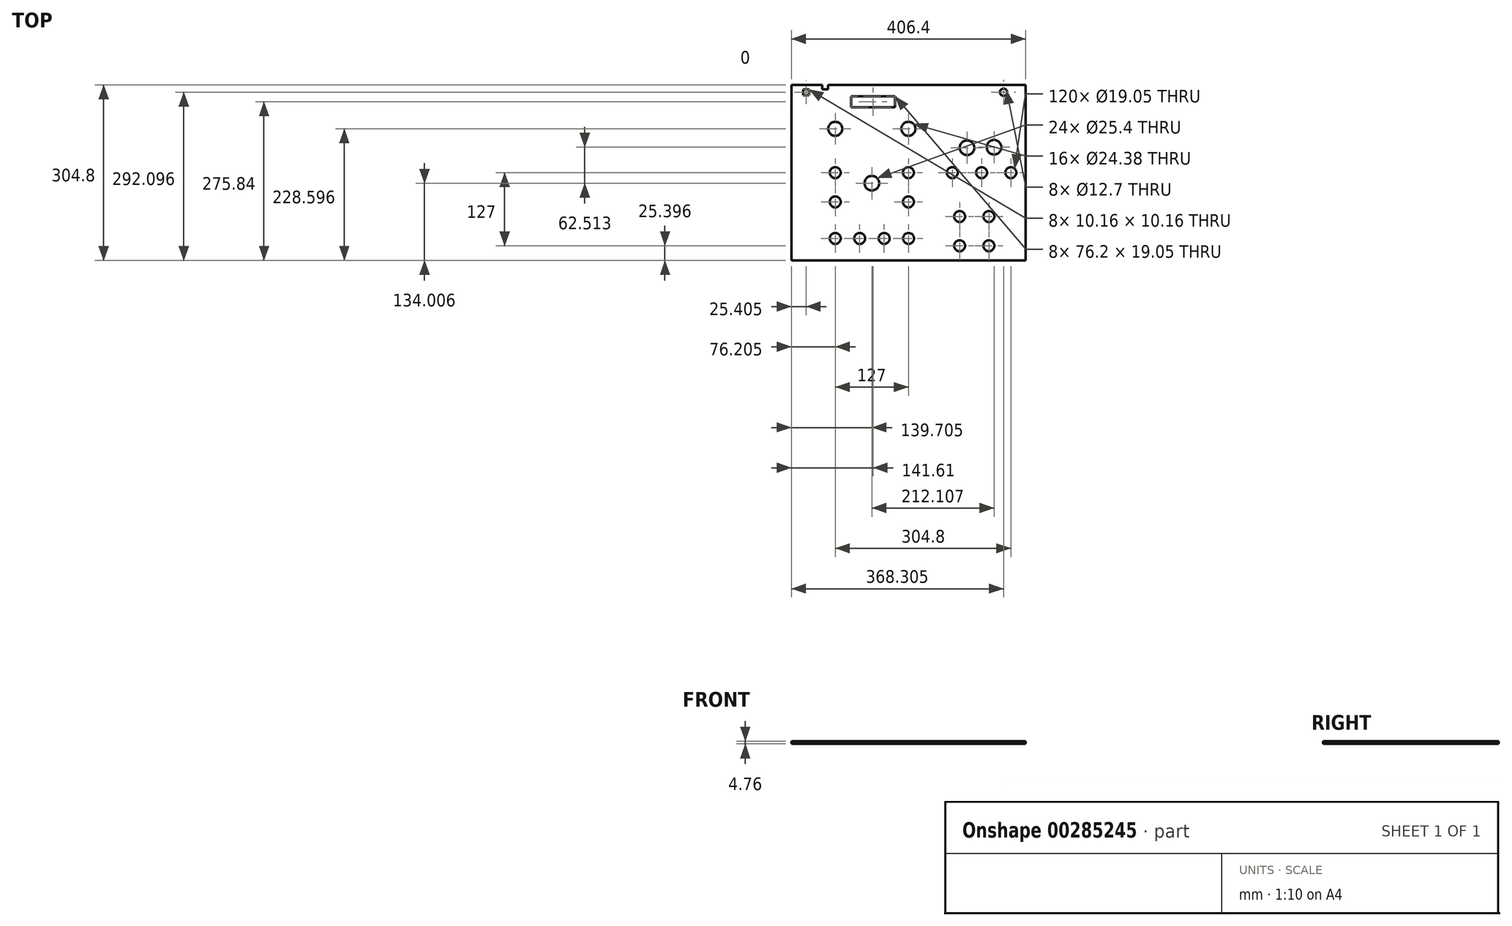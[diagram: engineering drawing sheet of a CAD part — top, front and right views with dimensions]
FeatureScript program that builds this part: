
annotation { "Feature Type Name" : "Feature", "Feature Type Description" : "" }
export const myFeature = defineFeature(function(context is Context, id is Id, definition is map)
    precondition{}
    {
        {
            var Q0;
            Q0=qCreatedBy(makeId("Top.planeOp"),FACE);
            var sketch = newSketch(context, id + "F0", { "sketchPlane" : qUnion([Q0])});
            skLineSegment(sketch, "E0.bottom", {"start": v(-218.92, 163.26) * mm, "end": v(187.48, 163.26) * mm});
            skLineSegment(sketch, "E0.top", {"start": v(-218.92, -141.54) * mm, "end": v(187.48, -141.54) * mm});
            skLineSegment(sketch, "E0.left", {"start": v(-218.92, 163.26) * mm, "end": v(-218.92, -141.54) * mm});
            skLineSegment(sketch, "E0.right", {"start": v(187.48, 163.26) * mm, "end": v(187.48, -141.54) * mm});
            skSolve(sketch);
        }
        {
            var Q0;
            Q0=makeQuery(id+"F0.imprint","IMPRINT",FACE,{"disambiguationData":[TD([[makeQuery(id+"F0.imprint","IMPRINT",EDGE,{"derivedFrom":sQuery(id+"F0.wireOp",EDGE,"E0.bottom")}),-1.0]])]});
            extrude(context, id + "F1", {"entities" : qUnion([Q0]), "depth" : 4.76 * mm});
        }
        {
            var Q0;
            Q0=qCreatedBy(makeId("Top.planeOp"),FACE);
            var sketch = newSketch(context, id + "F2", { "sketchPlane" : qUnion([Q0])});
            skCircle(sketch, "E1", {"center": v(-142.72, 87.06) * mm, "radius": 12.2 * mm});
            skLineSegment(sketch, "E2", {"start": v(-142.72, 87.06) * mm, "end": v(-142.72, -142.08) * mm, "construction": true});
            skCircle(sketch, "E3", {"center": v(-142.72, 10.86) * mm, "radius": 9.53 * mm});
            skCircle(sketch, "E4.0.1.0", {"center": v(-142.72, -39.94) * mm, "radius": 9.53 * mm});
            skLineSegment(sketch, "E4.direction2", {"start": v(-142.72, 10.86) * mm, "end": v(-142.72, -39.94) * mm, "construction": true});
            skCircle(sketch, "E5.1.0.0", {"center": v(-15.72, -39.94) * mm, "radius": 9.53 * mm});
            skCircle(sketch, "E5.1.0.2", {"center": v(-15.72, 10.86) * mm, "radius": 9.53 * mm});
            skLineSegment(sketch, "E5.1.0.3", {"start": v(-15.72, 87.06) * mm, "end": v(-15.72, -142.08) * mm, "construction": true});
            skLineSegment(sketch, "E5.1.0.5", {"start": v(-15.72, 10.86) * mm, "end": v(9.68, 10.86) * mm, "construction": true});
            skLineSegment(sketch, "E5.1.0.6", {"start": v(-15.72, 10.86) * mm, "end": v(-15.72, -39.94) * mm, "construction": true});
            skLineSegment(sketch, "E5.direction1", {"start": v(-142.72, -142.08) * mm, "end": v(-15.72, -142.08) * mm, "construction": true});
            skLineSegment(sketch, "E6.bottom", {"start": v(-165.58, 163.26) * mm, "end": v(-155.42, 163.26) * mm});
            skLineSegment(sketch, "E6.top", {"start": v(-165.58, 155.38) * mm, "end": v(-155.42, 155.38) * mm});
            skLineSegment(sketch, "E6.left", {"start": v(-165.58, 163.26) * mm, "end": v(-165.58, 155.38) * mm});
            skLineSegment(sketch, "E6.right", {"start": v(-155.42, 163.26) * mm, "end": v(-155.42, 155.38) * mm});
            skCircle(sketch, "E7.1.0.2", {"center": v(60.48, 10.86) * mm, "radius": 9.53 * mm});
            skLineSegment(sketch, "E7.direction1", {"start": v(-15.72, 10.86) * mm, "end": v(60.48, 10.86) * mm, "construction": true});
            skLineSegment(sketch, "E8.1.0.1", {"start": v(35.08, 10.86) * mm, "end": v(111.28, 10.86) * mm, "construction": true});
            skCircle(sketch, "E8.1.0.5", {"center": v(111.28, 10.86) * mm, "radius": 9.53 * mm});
            skLineSegment(sketch, "E8.2.0.1", {"start": v(85.88, 10.86) * mm, "end": v(162.08, 10.86) * mm, "construction": true});
            skCircle(sketch, "E8.2.0.5", {"center": v(162.08, 10.86) * mm, "radius": 9.53 * mm});
            skLineSegment(sketch, "E8.direction1", {"start": v(-15.72, 10.86) * mm, "end": v(35.08, 10.86) * mm, "construction": true});
            skCircle(sketch, "E9.1.0.5", {"center": v(86.05, 54.06) * mm, "radius": 12.7 * mm});
            skCircle(sketch, "E9.2.0.5", {"center": v(132.9, 54.98) * mm, "radius": 12.7 * mm});
            skCircle(sketch, "E10.MirrorC", {"center": v(-79.22, -7.53) * mm, "radius": 12.7 * mm});
            skCircle(sketch, "E11", {"center": v(149.38, 150.56) * mm, "radius": 6.35 * mm});
            skCircle(sketch, "E12", {"center": v(-52.55, 131.12) * mm, "radius": 3.18 * mm});
            skCircle(sketch, "E13.MirrorC", {"center": v(-103.35, 131.12) * mm, "radius": 3.18 * mm});
            skLineSegment(sketch, "E14.bottom", {"start": v(-198.6, 155.64) * mm, "end": v(-188.44, 155.64) * mm});
            skLineSegment(sketch, "E14.top", {"start": v(-198.6, 145.48) * mm, "end": v(-188.44, 145.48) * mm});
            skLineSegment(sketch, "E14.left", {"start": v(-198.6, 155.64) * mm, "end": v(-198.6, 145.48) * mm});
            skLineSegment(sketch, "E14.right", {"start": v(-188.44, 155.64) * mm, "end": v(-188.44, 145.48) * mm});
            skCircle(sketch, "E15", {"center": v(-15.72, 87.06) * mm, "radius": 12.2 * mm});
            skSolve(sketch);
        }
        {
            var Q0;
            Q0=qSketchRegion(id+"F2",true);
            extrude(context, id + "F3", {"entities" : qUnion([Q0]), "operationType" : NewBodyOperationType.REMOVE, "depth" : 25.4 * mm});
        }
        {
            var Q0;
            Q0=makeQuery(id+"F1.opExtrude","CAP_FACE",FACE,{"disambiguationData":[OSD([sQuery(id+"F0.wireOp",EDGE,"E0.bottom"),sQuery(id+"F0.wireOp",EDGE,"E0.top"),sQuery(id+"F0.wireOp",EDGE,"E0.left"),sQuery(id+"F0.wireOp",EDGE,"E0.right")])],"isStart":false});
            var sketch = newSketch(context, id + "F4", { "sketchPlane" : qUnion([Q0])});
            skCircle(sketch, "E16", {"center": v(-142.72, -103.44) * mm, "radius": 9.53 * mm});
            skCircle(sketch, "E17.1.0.0", {"center": v(-100.3, -103.44) * mm, "radius": 9.53 * mm});
            skLineSegment(sketch, "E17.direction1", {"start": v(-142.72, -103.44) * mm, "end": v(-100.3, -103.44) * mm, "construction": true});
            skCircle(sketch, "E18", {"center": v(73.18, -65.34) * mm, "radius": 9.53 * mm});
            skCircle(sketch, "E19.0.1.0", {"center": v(73.18, -116.14) * mm, "radius": 9.53 * mm});
            skCircle(sketch, "E19.1.0.0", {"center": v(123.98, -65.34) * mm, "radius": 9.53 * mm});
            skCircle(sketch, "E19.1.1.0", {"center": v(123.98, -116.14) * mm, "radius": 9.53 * mm});
            skLineSegment(sketch, "E19.direction1", {"start": v(73.18, -71.7) * mm, "end": v(123.98, -71.7) * mm, "construction": true});
            skLineSegment(sketch, "E19.direction2", {"start": v(73.18, -71.7) * mm, "end": v(73.18, -122.5) * mm, "construction": true});
            skCircle(sketch, "E20.0.2.0", {"center": v(-57.88, -103.44) * mm, "radius": 9.53 * mm});
            skCircle(sketch, "E20.0.3.0", {"center": v(-15.46, -103.44) * mm, "radius": 9.53 * mm});
            skLineSegment(sketch, "E21.bottom", {"start": v(-115.41, 143.82) * mm, "end": v(-39.21, 143.82) * mm});
            skLineSegment(sketch, "E21.top", {"start": v(-115.41, 124.77) * mm, "end": v(-39.21, 124.77) * mm});
            skLineSegment(sketch, "E21.left", {"start": v(-115.41, 143.82) * mm, "end": v(-115.41, 124.77) * mm});
            skLineSegment(sketch, "E21.right", {"start": v(-39.21, 143.82) * mm, "end": v(-39.21, 124.77) * mm});
            skSolve(sketch);
        }
        {
            var Q0;
            Q0=qSketchRegion(id+"F4",true);
            extrude(context, id + "F5", {"entities" : qUnion([Q0]), "operationType" : NewBodyOperationType.REMOVE, "oppositeDirection" : true, "depth" : 25.4 * mm});
        }
    });
